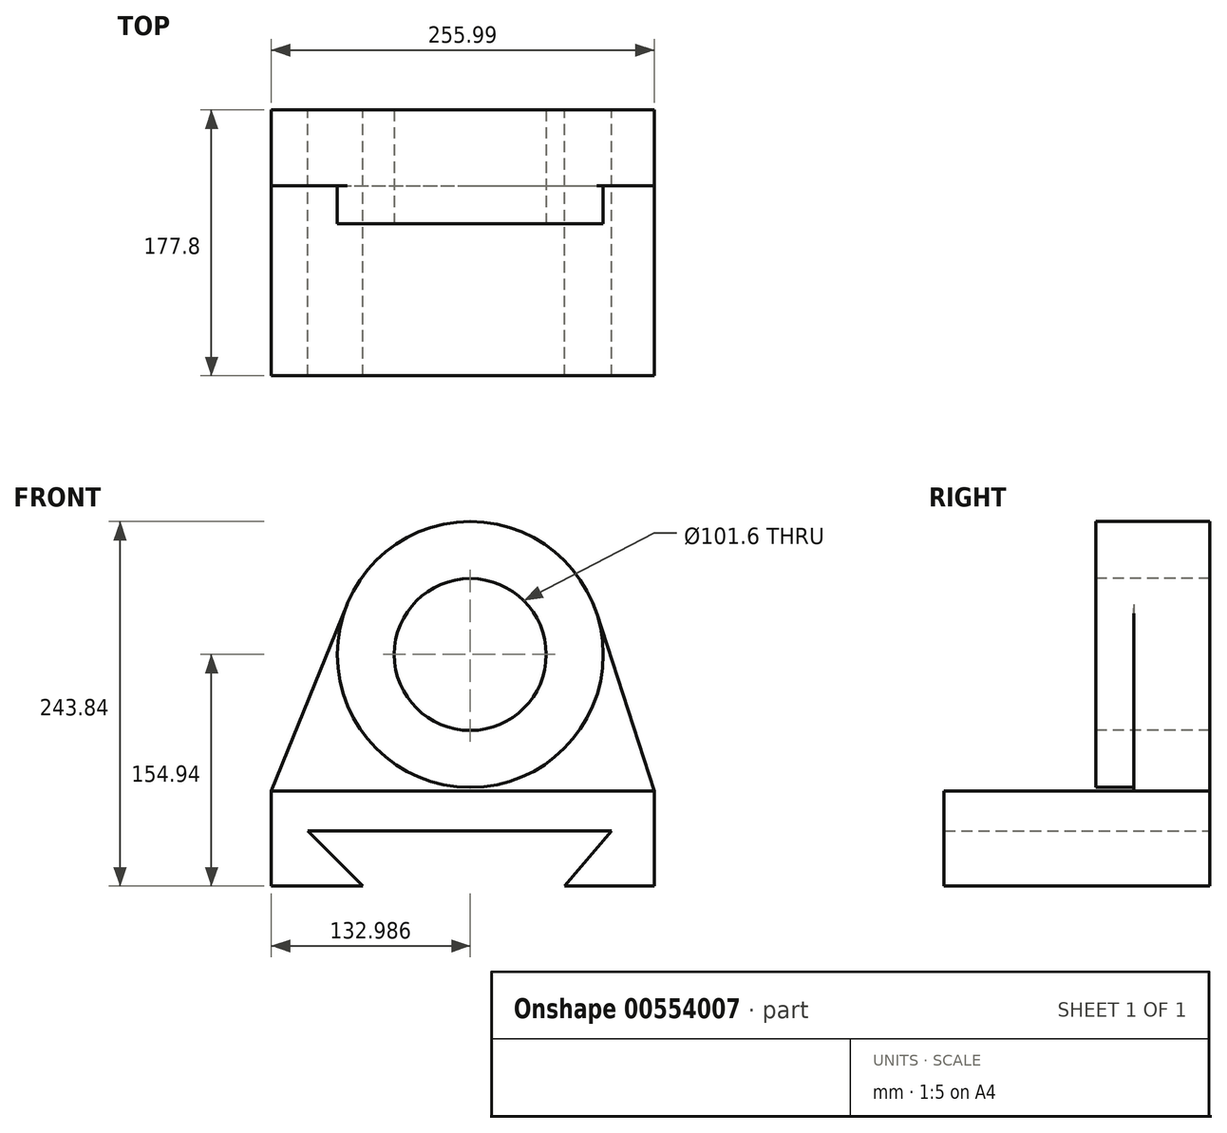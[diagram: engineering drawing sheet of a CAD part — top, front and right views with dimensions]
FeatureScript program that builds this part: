
annotation { "Feature Type Name" : "Feature", "Feature Type Description" : "" }
export const myFeature = defineFeature(function(context is Context, id is Id, definition is map)
    precondition{}
    {
        {
            var Q0;
            Q0=qCreatedBy(makeId("Front.planeOp"),FACE);
            var sketch = newSketch(context, id + "F0", { "sketchPlane" : qUnion([Q0])});
            skLineSegment(sketch, "E0", {"start": v(0, 63.5) * mm, "end": v(255.99, 63.5) * mm});
            skCircle(sketch, "E1", {"center": v(132.99, 154.94) * mm, "radius": 50.8 * mm});
            skLineSegment(sketch, "E2", {"start": v(255.99, 63.5) * mm, "end": v(255.99, 0) * mm});
            skLineSegment(sketch, "E3", {"start": v(255.99, 0) * mm, "end": v(196.17, 0) * mm});
            skLineSegment(sketch, "E4", {"start": v(227.4, 36.93) * mm, "end": v(196.17, 0) * mm});
            skLineSegment(sketch, "E5", {"start": v(0, 63.5) * mm, "end": v(0, 0) * mm});
            skLineSegment(sketch, "E6", {"start": v(0, 0) * mm, "end": v(61.13, 0) * mm});
            skLineSegment(sketch, "E7", {"start": v(61.13, 0) * mm, "end": v(24.2, 36.93) * mm});
            skLineSegment(sketch, "E8", {"start": v(24.2, 36.93) * mm, "end": v(227.4, 36.93) * mm});
            skLineSegment(sketch, "E9", {"start": v(0, 63.5) * mm, "end": v(50.6, 188.34) * mm});
            skLineSegment(sketch, "E10", {"start": v(255.99, 63.5) * mm, "end": v(215.62, 188.34) * mm});
            skCircle(sketch, "E11", {"center": v(132.99, 154.94) * mm, "radius": 88.9 * mm});
            skSolve(sketch);
        }
        {
            var Q0;
            Q0=makeQuery(id+"F0.imprint","IMPRINT",FACE,{"disambiguationData":[TD([[makeQuery(id+"F0.imprint","IMPRINT",EDGE,{"derivedFrom":sQuery(id+"F0.wireOp",EDGE,"E0")}),-1.0]])]});
            extrude(context, id + "F1", {"entities" : qUnion([Q0]), "depth" : 127 * mm, "offsetDistance" : 25.4 * mm});
        }
        {
            var Q0;
            {var subQ0=sQuery(id+"F0.wireOp",EDGE,"E0");Q0=makeQuery(id+"F0.imprint","IMPRINT",FACE,{"disambiguationData":[TD([[makeQuery(id+"F0.imprint","IMPRINT",EDGE,{"derivedFrom":subQ0}),1.0]])]});}
            var Q1;
            Q1=makeQuery(id+"F0.imprint","IMPRINT",FACE,{"disambiguationData":[TD([[makeQuery(id+"F0.imprint","IMPRINT",EDGE,{"derivedFrom":sQuery(id+"F0.wireOp",EDGE,"E1")}),-1.0]])]});
            var Q2;
            Q2=makeQuery(id+"F0.imprint","IMPRINT",FACE,{"disambiguationData":[TD([[makeQuery(id+"F0.imprint","IMPRINT",EDGE,{"derivedFrom":sQuery(id+"F0.wireOp",EDGE,"E0")}),-1.0]])]});
            extrude(context, id + "F2", {"entities" : qUnion([Q0, Q1, Q2]), "operationType" : NewBodyOperationType.ADD, "oppositeDirection" : true, "depth" : 50.8 * mm, "offsetDistance" : 25.4 * mm});
        }
        {
            var Q0;
            Q0=makeQuery(id+"F0.imprint","IMPRINT",FACE,{"disambiguationData":[TD([[makeQuery(id+"F0.imprint","IMPRINT",EDGE,{"derivedFrom":sQuery(id+"F0.wireOp",EDGE,"E1")}),-1.0]])]});
            extrude(context, id + "F3", {"entities" : qUnion([Q0]), "operationType" : NewBodyOperationType.ADD, "depth" : 25.4 * mm, "offsetDistance" : 25.4 * mm});
        }
    });
